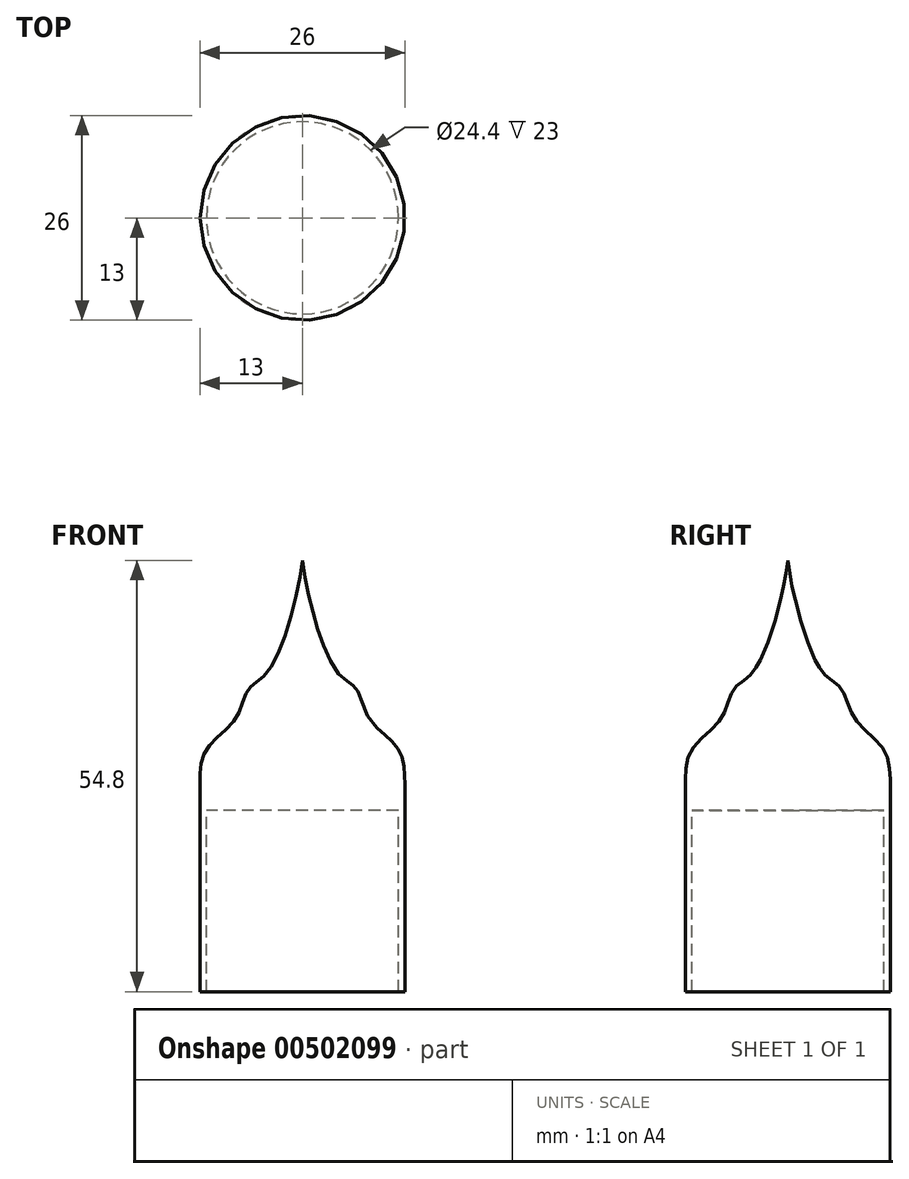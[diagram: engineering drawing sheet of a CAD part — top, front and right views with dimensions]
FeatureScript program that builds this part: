
annotation { "Feature Type Name" : "Feature", "Feature Type Description" : "" }
export const myFeature = defineFeature(function(context is Context, id is Id, definition is map)
    precondition{}
    {
        {
            var Q0;
            Q0=qCreatedBy(makeId("Front.planeOp"),FACE);
            var sketch = newSketch(context, id + "F0", { "sketchPlane" : qUnion([Q0])});
            skLineSegment(sketch, "E0", {"start": v(-13, 0) * mm, "end": v(-13, 23) * mm});
            skLineSegment(sketch, "E1", {"start": v(-12.2, 0) * mm, "end": v(-12.2, 23) * mm});
            skLineSegment(sketch, "E2", {"start": v(-13, 0) * mm, "end": v(-12.2, 0) * mm});
            skFitSpline(sketch, "E3", {"points": [v(-13, 23) * mm, v(-13, 26.69) * mm, v(-12.2, 30.77) * mm, v(-8.53, 34.63) * mm, v(-6.81, 38.5) * mm, v(-4.24, 40.85) * mm, v(0, 54.8) * mm, v(0, 59.3) * mm], "startDerivative": vector(-0.1, 30.15) * mm, "endDerivative": vector(-3.07, 26.35) * mm});
            skLineSegment(sketch, "E4", {"start": v(-12.2, 23) * mm, "end": v(0, 23) * mm});
            skLineSegment(sketch, "E5", {"start": v(0, 62.3) * mm, "end": v(0, -2.5) * mm});
            skSolve(sketch);
        }
        {
            var Q0;
            {var subQ1=sQuery(id+"F0.wireOp",EDGE,"E0");Q0=makeQuery(id+"F0.imprint","IMPRINT",FACE,{"disambiguationData":[TD([[makeQuery(id+"F0.imprint","IMPRINT",EDGE,{"derivedFrom":subQ1}),-1.0]])]});}
            var Q1;
            Q1=sQuery(id+"F0.wireOp",EDGE,"E5");
            revolve(context, id + "F1", {"entities" : qUnion([Q0]), "axis" : qUnion([Q1]), "revolveType" : RevolveType.FULL});
        }
    });
